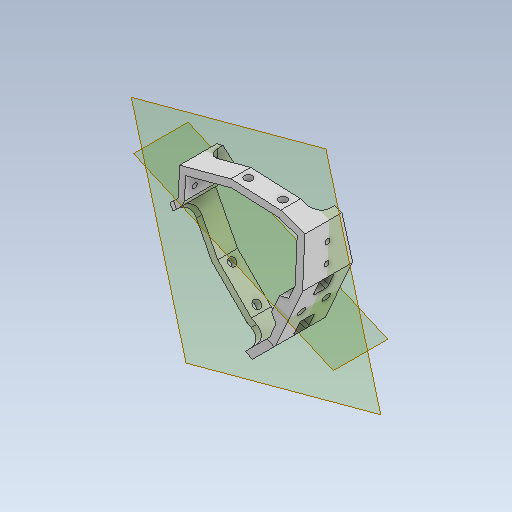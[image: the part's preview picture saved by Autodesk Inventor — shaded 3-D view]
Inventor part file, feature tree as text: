
AUTODESK INVENTOR PART (.ipt)
format: ipt  version: 2020 (Build 240168000, 168)  size: 299,008 bytes
history: native  units: mm
features: sketch x15, plane x4, other x3
ambient origin geometry x8: Origin, YZ Plane, XZ Plane, XY Plane, X Axis, Y Axis, Z Axis, Center Point
bodies: Solid1 (feature_tree)
feature tree (22):
  other  "leg_holder_2.ipt"
  other  "Solid2::leg_holder_2.ipt"
  other  "TaggingFeature1"
  sketch  "Sketch1"  dims[d0=10.0mm]
  sketch  "Sketch4"
  sketch  "Sketch5"
  sketch  "Sketch6"
  sketch  "Sketch7"
  sketch  "Sketch8"
  sketch  "Sketch10"
  sketch  "Sketch11"
  sketch  "Sketch12"
  sketch  "Sketch13"
  sketch  "Sketch14"
  sketch  "Sketch15"
  sketch  "Sketch18"
  sketch  "Sketch19"
  sketch  "Sketch20"
  plane  "Work Plane1"
  plane  "Work Plane2"
  plane  "Work Plane3"
  plane  "Work Plane4"
